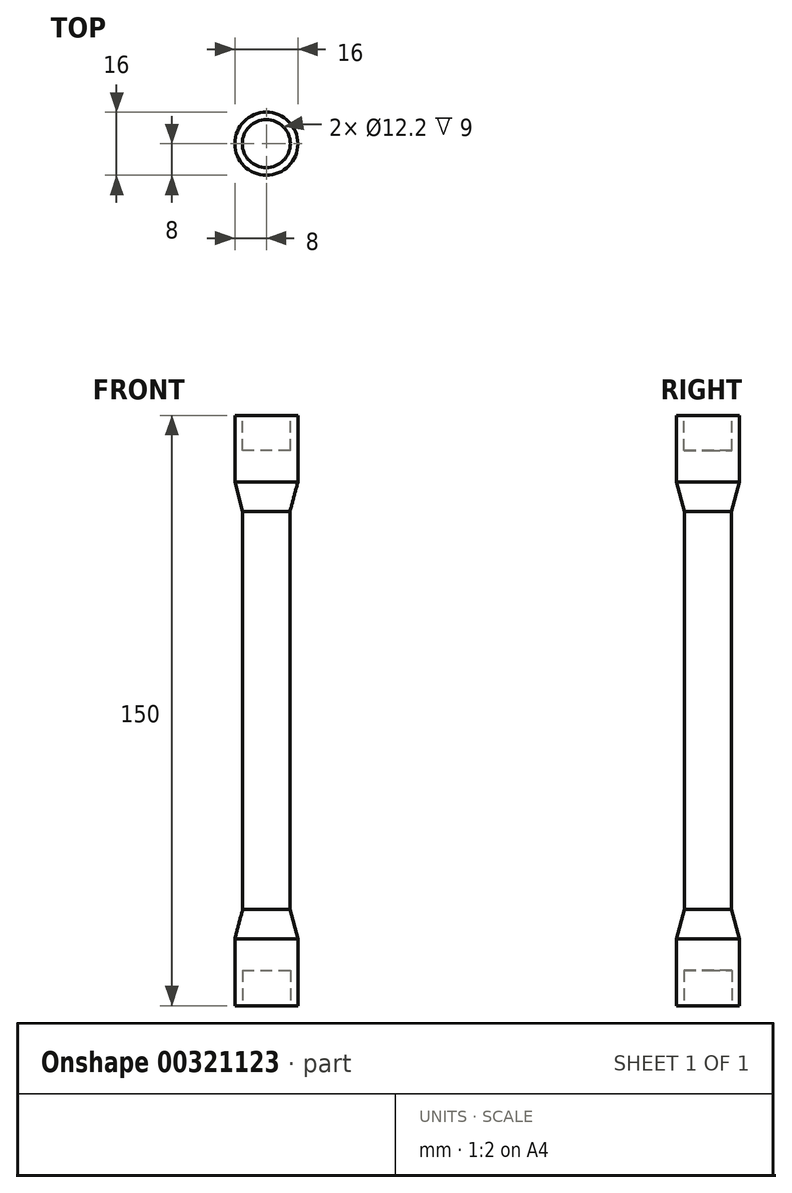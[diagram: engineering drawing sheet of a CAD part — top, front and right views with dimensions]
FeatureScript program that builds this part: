
annotation { "Feature Type Name" : "Feature", "Feature Type Description" : "" }
export const myFeature = defineFeature(function(context is Context, id is Id, definition is map)
    precondition{}
    {
        {
            var Q0;
            Q0=qCreatedBy(makeId("Top.planeOp"),FACE);
            var sketch = newSketch(context, id + "F0", { "sketchPlane" : qUnion([Q0])});
            skCircle(sketch, "E0", {"center": v(0, 0) * mm, "radius": 6 * mm});
            skSolve(sketch);
        }
        {
            var Q0;
            Q0=makeQuery(id+"F0.imprint","IMPRINT",FACE,{"disambiguationData":[TD([[makeQuery(id+"F0.imprint","IMPRINT",EDGE,{"derivedFrom":sQuery(id+"F0.wireOp",EDGE,"E0")}),1.0]])]});
            extrude(context, id + "F1", {"entities" : qUnion([Q0]), "depth" : 50 * mm, "hasSecondDirection" : true, "secondDirectionOppositeDirection" : true, "secondDirectionDepth" : 50 * mm});
        }
        {
            var Q0;
            Q0=makeQuery(id+"F1.opExtrude","CAP_FACE",FACE,{"disambiguationData":[OSD([sQuery(id+"F0.wireOp",EDGE,"E0")])],"isStart":false});
            var sketch = newSketch(context, id + "F2", { "sketchPlane" : qUnion([Q0])});
            skCircle(sketch, "E1", {"center": v(0, 0) * mm, "radius": 8 * mm});
            skSolve(sketch);
        }
        {
            var Q0;
            Q0=makeQuery(id+"F1.opExtrude","CAP_FACE",FACE,{"disambiguationData":[OSD([sQuery(id+"F0.wireOp",EDGE,"E0")])],"isStart":true});
            var sketch = newSketch(context, id + "F3", { "sketchPlane" : qUnion([Q0])});
            skCircle(sketch, "E2", {"center": v(0, 0) * mm, "radius": 8 * mm});
            skSolve(sketch);
        }
        {
            var Q0;
            Q0=makeQuery(id+"F2.imprint","IMPRINT",FACE,{"disambiguationData":[TD([[makeQuery(id+"F2.imprint","IMPRINT",EDGE,{"derivedFrom":sQuery(id+"F2.wireOp",EDGE,"E1")}),1.0]])]});
            var Q1;
            Q1=makeQuery(id+"F2.imprint","IMPRINT",FACE,{"disambiguationData":[TD([[makeQuery(id+"F2.imprint","IMPRINT",EDGE,{"derivedFrom":makeQuery(id+"F1.opExtrude","CAP_EDGE",EDGE,{"disambiguationData":[OSD([sQuery(id+"F0.wireOp",EDGE,"E0")])],"isStart":false})}),1.0]])]});
            extrude(context, id + "F4", {"entities" : qUnion([Q0, Q1]), "operationType" : NewBodyOperationType.ADD, "depth" : 25 * mm});
        }
        {
            var Q0;
            Q0=makeQuery(id+"F3.imprint","IMPRINT",FACE,{"disambiguationData":[TD([[makeQuery(id+"F3.imprint","IMPRINT",EDGE,{"derivedFrom":makeQuery(id+"F1.opExtrude","CAP_EDGE",EDGE,{"disambiguationData":[OSD([sQuery(id+"F0.wireOp",EDGE,"E0")])],"isStart":true})}),-1.0]])]});
            var Q1;
            Q1=makeQuery(id+"F3.imprint","IMPRINT",FACE,{"disambiguationData":[TD([[makeQuery(id+"F3.imprint","IMPRINT",EDGE,{"derivedFrom":sQuery(id+"F3.wireOp",EDGE,"E2")}),1.0]])]});
            extrude(context, id + "F5", {"entities" : qUnion([Q0, Q1]), "operationType" : NewBodyOperationType.ADD, "depth" : 25 * mm});
        }
        {
            var Q0;
            Q0=makeQuery(id+"F5.opExtrude","CAP_EDGE",EDGE,{"disambiguationData":[OSD([sQuery(id+"F3.wireOp",EDGE,"E2")])],"isStart":true});
            var Q1;
            Q1=makeQuery(id+"F4.opExtrude","CAP_EDGE",EDGE,{"disambiguationData":[OSD([sQuery(id+"F2.wireOp",EDGE,"E1")])],"isStart":true});
            chamfer(context, id + "F6", {"entities" : qUnion([Q0, Q1]), "chamferType" : ChamferType.OFFSET_ANGLE, "width" : 8 * mm, "oppositeDirection" : false, "angle" : 15 * degree, "tangentPropagation" : true});
        }
        {
            var Q0;
            Q0=makeQuery(id+"F5.opExtrude","CAP_FACE",FACE,{"disambiguationData":[OSD([sQuery(id+"F3.wireOp",EDGE,"E2")])],"isStart":false});
            var sketch = newSketch(context, id + "F7", { "sketchPlane" : qUnion([Q0])});
            skCircle(sketch, "E3", {"center": v(0, 0) * mm, "radius": 6.1 * mm});
            skSolve(sketch);
        }
        {
            var Q0;
            Q0=makeQuery(id+"F7.imprint","IMPRINT",FACE,{"disambiguationData":[TD([[makeQuery(id+"F7.imprint","IMPRINT",EDGE,{"derivedFrom":sQuery(id+"F7.wireOp",EDGE,"E3")}),1.0]])]});
            extrude(context, id + "F8", {"entities" : qUnion([Q0]), "operationType" : NewBodyOperationType.REMOVE, "oppositeDirection" : true, "depth" : 9 * mm});
        }
        {
            var Q0;
            Q0=makeQuery(id+"F4.opExtrude","CAP_FACE",FACE,{"disambiguationData":[OSD([sQuery(id+"F2.wireOp",EDGE,"E1")])],"isStart":false});
            var sketch = newSketch(context, id + "F9", { "sketchPlane" : qUnion([Q0])});
            skCircle(sketch, "E4", {"center": v(0, 0) * mm, "radius": 6.1 * mm});
            skSolve(sketch);
        }
        {
            var Q0;
            Q0=makeQuery(id+"F9.imprint","IMPRINT",FACE,{"disambiguationData":[TD([[makeQuery(id+"F9.imprint","IMPRINT",EDGE,{"derivedFrom":sQuery(id+"F9.wireOp",EDGE,"E4")}),1.0]])]});
            extrude(context, id + "F10", {"entities" : qUnion([Q0]), "operationType" : NewBodyOperationType.REMOVE, "oppositeDirection" : true, "depth" : 9 * mm});
        }
    });
